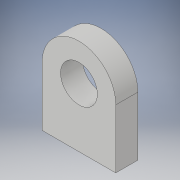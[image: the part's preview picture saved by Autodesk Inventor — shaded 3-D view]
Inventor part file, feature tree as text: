
AUTODESK INVENTOR PART (.ipt)
format: ipt  version: 2019.4 (Build 234330000, 330)  size: 102,400 bytes
history: native  units: mm
features: extrude x1, sketch x1
ambient origin geometry x8: Origin, YZ Plane, XZ Plane, XY Plane, X Axis, Y Axis, Z Axis, Center Point
bodies: Body1 (feature_tree)
feature tree (2):
  extrude  "Extrusión2"  Depth=250.0mm
  sketch  "Boceto2"  dims[d7=500.0mm d8=250.0mm d9=400.0mm d10=500.0mm d11=150.0mm d12=0.0mm]
